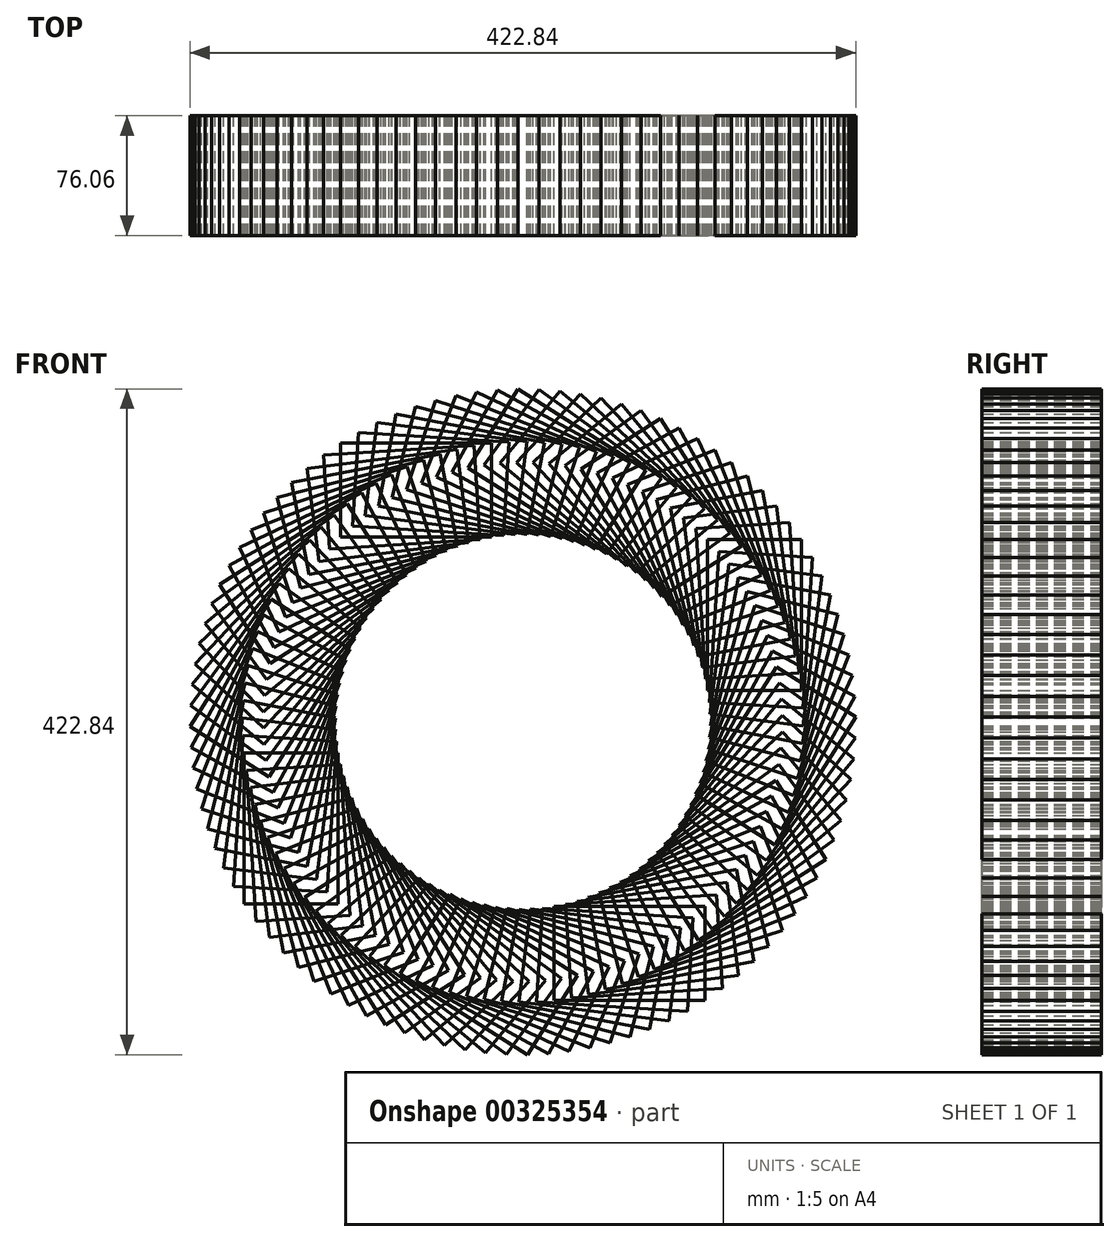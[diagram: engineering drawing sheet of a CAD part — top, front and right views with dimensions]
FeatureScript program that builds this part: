
annotation { "Feature Type Name" : "Feature", "Feature Type Description" : "" }
export const myFeature = defineFeature(function(context is Context, id is Id, definition is map)
    precondition{}
    {
        {
            var Q0;
            Q0=qCreatedBy(makeId("Front.planeOp"),FACE);
            var sketch = newSketch(context, id + "F0", { "sketchPlane" : qUnion([Q0])});
            skLineSegment(sketch, "E0.bottom", {"start": v(-138.78, 72.74) * mm, "end": v(-42.82, 72.74) * mm});
            skLineSegment(sketch, "E0.top", {"start": v(-138.78, 13.19) * mm, "end": v(-42.82, 13.19) * mm});
            skLineSegment(sketch, "E0.left", {"start": v(-138.78, 72.74) * mm, "end": v(-138.78, 13.19) * mm});
            skLineSegment(sketch, "E0.right", {"start": v(-42.82, 72.74) * mm, "end": v(-42.82, 13.19) * mm});
            skPoint(sketch, "E0.middle", {"position": v(-90.8, 42.96) * mm});
            skSolve(sketch);
        }
        {
            var Q0;
            Q0=makeQuery(id+"F0.imprint","IMPRINT",FACE,{"disambiguationData":[TD([[makeQuery(id+"F0.imprint","IMPRINT",EDGE,{"derivedFrom":sQuery(id+"F0.wireOp",EDGE,"E0.bottom")}),-1.0]])]});
            var Q1;
            Q1 = qSketchRegion(id + "F0", true);
            extrude(context, id + "F1", {"entities" : qUnion([Q0, Q1]), "depth" : 76.06 * mm, "offsetDistance" : 25.4 * mm});
        }
        {
            var Q0;
            Q0=makeQuery(id+"F1.opExtrude","CAP_FACE",FACE,{"disambiguationData":[OSD([sQuery(id+"F0.wireOp",EDGE,"E0.bottom"),sQuery(id+"F0.wireOp",EDGE,"E0.top"),sQuery(id+"F0.wireOp",EDGE,"E0.left"),sQuery(id+"F0.wireOp",EDGE,"E0.right")])],"isStart":false});
            var sketch = newSketch(context, id + "F2", { "sketchPlane" : qUnion([Q0])});
            skCircle(sketch, "E1", {"center": v(-23, -104.2) * mm, "radius": 22.68 * mm});
            skSolve(sketch);
        }
        {
            var Q0;
            Q0=sQuery(id+"F2.wireOp",EDGE,"E1");
            extrude(context, id + "F3", {"bodyType" : ToolBodyType.SURFACE, "surfaceEntities" : qUnion([Q0]), "depth" : 118.65 * mm, "offsetDistance" : 25.4 * mm, "hasSecondDirection" : true, "secondDirectionOppositeDirection" : true, "secondDirectionDepth" : 67.83 * mm});
        }
        {
            var Q0;
            Q0=makeQuery(id+"F1.opExtrude","SWEPT_BODY",BODY,{"disambiguationData":[OSD([sQuery(id+"F0.wireOp",EDGE,"E0.bottom"),sQuery(id+"F0.wireOp",EDGE,"E0.top"),sQuery(id+"F0.wireOp",EDGE,"E0.left"),sQuery(id+"F0.wireOp",EDGE,"E0.right")])]});
            var Q1;
            Q1=makeQuery(id+"F3.opExtrude","SWEPT_FACE",FACE,{"disambiguationData":[OSD([sQuery(id+"F2.wireOp",EDGE,"E1")])]});
            circularPattern(context, id + "F4", {"entities" : qUnion([Q0]), "axis" : qUnion([Q1]), "angle" : 360 * degree, "instanceCount" : 100, "equalSpace" : true});
        }
    });
